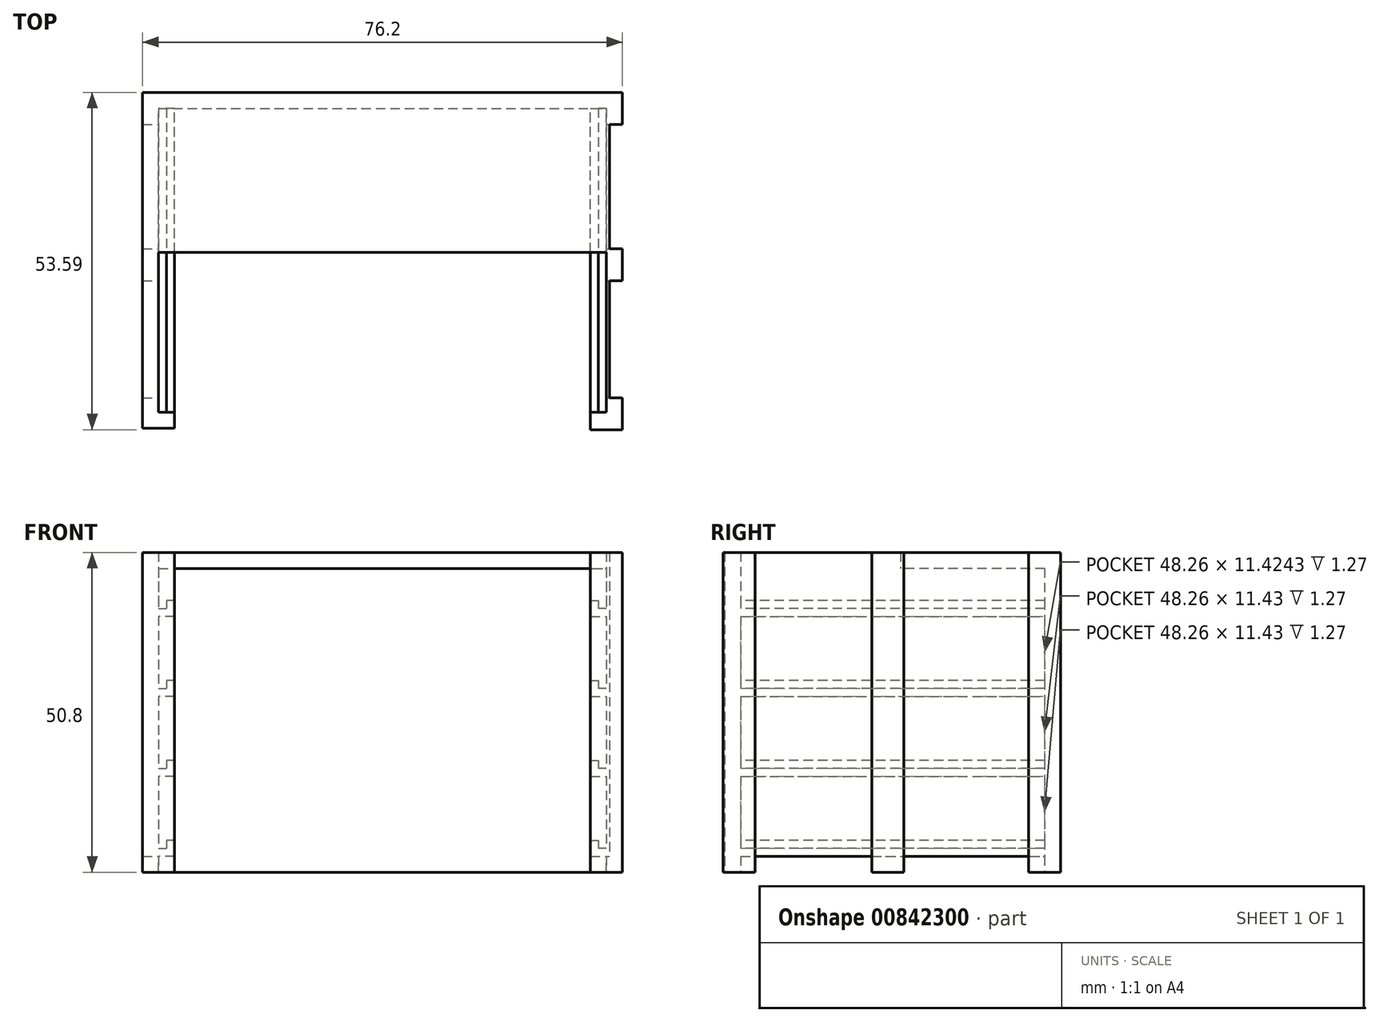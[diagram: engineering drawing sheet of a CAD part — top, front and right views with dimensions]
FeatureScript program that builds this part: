
annotation { "Feature Type Name" : "Feature", "Feature Type Description" : "" }
export const myFeature = defineFeature(function(context is Context, id is Id, definition is map)
    precondition{}
    {
        {
            var Q0;
            Q0=qCreatedBy(makeId("Front.planeOp"),FACE);
            var sketch = newSketch(context, id + "F0", { "sketchPlane" : qUnion([Q0])});
            skLineSegment(sketch, "E0.bottom", {"start": v(-38.1, 29.8) * mm, "end": v(38.1, 29.8) * mm});
            skLineSegment(sketch, "E0.top", {"start": v(-38.1, -21) * mm, "end": v(38.1, -21) * mm});
            skLineSegment(sketch, "E0.left", {"start": v(-38.1, 29.8) * mm, "end": v(-38.1, -21) * mm});
            skLineSegment(sketch, "E0.right", {"start": v(38.1, 29.8) * mm, "end": v(38.1, -21) * mm});
            skSolve(sketch);
        }
        {
            var Q0;
            Q0 = qSketchRegion(id + "F0", true);
            extrude(context, id + "F1", {"entities" : qUnion([Q0]), "depth" : 25.4 * mm, "offsetDistance" : 25.4 * mm, "hasSecondDirection" : true, "secondDirectionOppositeDirection" : true, "secondDirectionDepth" : 25.4 * mm});
        }
        {
            var Q0;
            Q0=makeQuery(id+"F1.opExtrude","CAP_FACE",FACE,{"disambiguationData":[OSD([sQuery(id+"F0.wireOp",EDGE,"E0.bottom"),sQuery(id+"F0.wireOp",EDGE,"E0.top"),sQuery(id+"F0.wireOp",EDGE,"E0.left"),sQuery(id+"F0.wireOp",EDGE,"E0.right")])],"isStart":false});
            var sketch = newSketch(context, id + "F2", { "sketchPlane" : qUnion([Q0])});
            skLineSegment(sketch, "E1.bottom", {"start": v(-35.56, 29.8) * mm, "end": v(35.56, 29.8) * mm});
            skLineSegment(sketch, "E1.top", {"start": v(-35.56, -21) * mm, "end": v(35.56, -21) * mm});
            skLineSegment(sketch, "E1.left", {"start": v(-35.56, 29.8) * mm, "end": v(-35.56, -21) * mm});
            skLineSegment(sketch, "E1.right", {"start": v(35.56, 29.8) * mm, "end": v(35.56, -21) * mm});
            skSolve(sketch);
        }
        {
            var Q0;
            Q0 = qSketchRegion(id + "F2", true);
            extrude(context, id + "F3", {"entities" : qUnion([Q0]), "operationType" : NewBodyOperationType.REMOVE, "oppositeDirection" : true, "depth" : 25.4 * mm, "offsetDistance" : 25.4 * mm});
        }
        {
            var Q0;
            Q0=makeQuery(id+"F3.boolean.opBoolean","COPY",FACE,{"derivedFrom":makeQuery(id+"F3.opExtrude","CAP_FACE",FACE,{"disambiguationData":[OSD([sQuery(id+"F2.wireOp",EDGE,"E1.bottom"),sQuery(id+"F2.wireOp",EDGE,"E1.top"),sQuery(id+"F2.wireOp",EDGE,"E1.left"),sQuery(id+"F2.wireOp",EDGE,"E1.right")])],"isStart":false})});
            var sketch = newSketch(context, id + "F4", { "sketchPlane" : qUnion([Q0])});
            skLineSegment(sketch, "E2.bottom", {"start": v(-35.56, 27.25) * mm, "end": v(35.56, 27.25) * mm});
            skLineSegment(sketch, "E2.top", {"start": v(-35.56, -21) * mm, "end": v(35.56, -21) * mm});
            skLineSegment(sketch, "E2.left", {"start": v(-35.56, 27.25) * mm, "end": v(-35.56, -21) * mm});
            skLineSegment(sketch, "E2.right", {"start": v(35.56, 27.25) * mm, "end": v(35.56, -21) * mm});
            skSolve(sketch);
        }
        {
            var Q0;
            Q0 = qSketchRegion(id + "F4", true);
            extrude(context, id + "F5", {"entities" : qUnion([Q0]), "operationType" : NewBodyOperationType.REMOVE, "oppositeDirection" : true, "depth" : 22.86 * mm, "offsetDistance" : 25.4 * mm});
        }
        {
            var Q0;
            Q0=makeQuery(id+"F5.boolean.opBoolean","MERGE",FACE,{"derivedFrom":[makeQuery(id+"F3.boolean.opBoolean","COPY",FACE,{"derivedFrom":makeQuery(id+"F3.opExtrude","SWEPT_FACE",FACE,{"disambiguationData":[OSD([sQuery(id+"F2.wireOp",EDGE,"E1.left")])]})}),makeQuery(id+"F5.opExtrude","SWEPT_FACE",FACE,{"disambiguationData":[OSD([sQuery(id+"F4.wireOp",EDGE,"E2.left")])]})]});
            var sketch = newSketch(context, id + "F6", { "sketchPlane" : qUnion([Q0])});
            skLineSegment(sketch, "E3.bottom", {"start": v(-25.4, -15.93) * mm, "end": v(22.86, -15.93) * mm});
            skLineSegment(sketch, "E3.top", {"start": v(-25.4, -18.47) * mm, "end": v(22.86, -18.47) * mm});
            skLineSegment(sketch, "E3.left", {"start": v(-25.4, -15.93) * mm, "end": v(-25.4, -18.47) * mm});
            skLineSegment(sketch, "E3.right", {"start": v(22.86, -15.93) * mm, "end": v(22.86, -18.47) * mm});
            skSolve(sketch);
        }
        {
            var Q0;
            Q0 = qSketchRegion(id + "F6", true);
            extrude(context, id + "F7", {"entities" : qUnion([Q0]), "operationType" : NewBodyOperationType.ADD, "depth" : 2.54 * mm, "offsetDistance" : 25.4 * mm});
        }
        {
            var Q0;
            {var subQ0=sQuery(id+"F2.wireOp",EDGE,"E1.left");var subQ1=sQuery(id+"F0.wireOp",EDGE,"E0.bottom");var subQ2=sQuery(id+"F4.wireOp",EDGE,"E2.left");Q0=makeQuery(id+"F7.boolean.opBoolean","SPLIT",FACE,{"disambiguationData":[TD([makeQuery(id+"F1.opExtrude","SWEPT_FACE",FACE,{"disambiguationData":[OSD([subQ1])]})])],"derivedFrom":makeQuery(id+"F5.boolean.opBoolean","MERGE",FACE,{"derivedFrom":[makeQuery(id+"F3.boolean.opBoolean","COPY",FACE,{"derivedFrom":makeQuery(id+"F3.opExtrude","SWEPT_FACE",FACE,{"disambiguationData":[OSD([subQ0])]})}),makeQuery(id+"F5.opExtrude","SWEPT_FACE",FACE,{"disambiguationData":[OSD([subQ2])]})]})});}
            var sketch = newSketch(context, id + "F8", { "sketchPlane" : qUnion([Q0])});
            skLineSegment(sketch, "E4.bottom", {"start": v(-25.4, -3.23) * mm, "end": v(22.86, -3.23) * mm});
            skLineSegment(sketch, "E4.top", {"start": v(-25.4, -5.77) * mm, "end": v(22.86, -5.77) * mm});
            skLineSegment(sketch, "E4.left", {"start": v(-25.4, -3.23) * mm, "end": v(-25.4, -5.77) * mm});
            skLineSegment(sketch, "E4.right", {"start": v(22.86, -3.23) * mm, "end": v(22.86, -5.77) * mm});
            skSolve(sketch);
        }
        {
            var Q0;
            Q0 = qSketchRegion(id + "F8", true);
            extrude(context, id + "F9", {"entities" : qUnion([Q0]), "operationType" : NewBodyOperationType.ADD, "depth" : 2.54 * mm, "offsetDistance" : 25.4 * mm});
        }
        {
            var Q0;
            {var subQ0=sQuery(id+"F2.wireOp",EDGE,"E1.left");var subQ2=sQuery(id+"F0.wireOp",EDGE,"E0.bottom");var subQ4=sQuery(id+"F4.wireOp",EDGE,"E2.left");var subQ8=makeQuery(id+"F1.opExtrude","SWEPT_FACE",FACE,{"disambiguationData":[OSD([subQ2])]});Q0=makeQuery(id+"F9.boolean.opBoolean","SPLIT",FACE,{"disambiguationData":[TD([subQ8])],"derivedFrom":makeQuery(id+"F7.boolean.opBoolean","SPLIT",FACE,{"disambiguationData":[TD([subQ8])],"derivedFrom":makeQuery(id+"F5.boolean.opBoolean","MERGE",FACE,{"derivedFrom":[makeQuery(id+"F3.boolean.opBoolean","COPY",FACE,{"derivedFrom":makeQuery(id+"F3.opExtrude","SWEPT_FACE",FACE,{"disambiguationData":[OSD([subQ0])]})}),makeQuery(id+"F5.opExtrude","SWEPT_FACE",FACE,{"disambiguationData":[OSD([subQ4])]})]})})});}
            var sketch = newSketch(context, id + "F10", { "sketchPlane" : qUnion([Q0])});
            skLineSegment(sketch, "E5.bottom", {"start": v(-25.4, 9.47) * mm, "end": v(22.86, 9.47) * mm});
            skLineSegment(sketch, "E5.top", {"start": v(-25.4, 6.93) * mm, "end": v(22.86, 6.93) * mm});
            skLineSegment(sketch, "E5.left", {"start": v(-25.4, 9.47) * mm, "end": v(-25.4, 6.93) * mm});
            skLineSegment(sketch, "E5.right", {"start": v(22.86, 9.47) * mm, "end": v(22.86, 6.93) * mm});
            skSolve(sketch);
        }
        {
            var Q0;
            Q0 = qSketchRegion(id + "F10", true);
            extrude(context, id + "F11", {"entities" : qUnion([Q0]), "operationType" : NewBodyOperationType.ADD, "depth" : 2.54 * mm, "offsetDistance" : 25.4 * mm});
        }
        {
            var Q0;
            {var subQ0=sQuery(id+"F2.wireOp",EDGE,"E1.left");var subQ2=sQuery(id+"F0.wireOp",EDGE,"E0.bottom");var subQ4=sQuery(id+"F4.wireOp",EDGE,"E2.left");var subQ8=makeQuery(id+"F1.opExtrude","SWEPT_FACE",FACE,{"disambiguationData":[OSD([subQ2])]});Q0=makeQuery(id+"F11.boolean.opBoolean","SPLIT",FACE,{"disambiguationData":[TD([subQ8])],"derivedFrom":makeQuery(id+"F9.boolean.opBoolean","SPLIT",FACE,{"disambiguationData":[TD([subQ8])],"derivedFrom":makeQuery(id+"F7.boolean.opBoolean","SPLIT",FACE,{"disambiguationData":[TD([subQ8])],"derivedFrom":makeQuery(id+"F5.boolean.opBoolean","MERGE",FACE,{"derivedFrom":[makeQuery(id+"F3.boolean.opBoolean","COPY",FACE,{"derivedFrom":makeQuery(id+"F3.opExtrude","SWEPT_FACE",FACE,{"disambiguationData":[OSD([subQ0])]})}),makeQuery(id+"F5.opExtrude","SWEPT_FACE",FACE,{"disambiguationData":[OSD([subQ4])]})]})})})});}
            var sketch = newSketch(context, id + "F12", { "sketchPlane" : qUnion([Q0])});
            skLineSegment(sketch, "E6.bottom", {"start": v(-25.4, 22.17) * mm, "end": v(22.86, 22.17) * mm});
            skLineSegment(sketch, "E6.top", {"start": v(-25.4, 19.63) * mm, "end": v(22.86, 19.63) * mm});
            skLineSegment(sketch, "E6.left", {"start": v(-25.4, 22.17) * mm, "end": v(-25.4, 19.63) * mm});
            skLineSegment(sketch, "E6.right", {"start": v(22.86, 22.17) * mm, "end": v(22.86, 19.63) * mm});
            skSolve(sketch);
        }
        {
            var Q0;
            Q0 = qSketchRegion(id + "F12", true);
            extrude(context, id + "F13", {"entities" : qUnion([Q0]), "operationType" : NewBodyOperationType.ADD, "depth" : 2.54 * mm, "offsetDistance" : 25.4 * mm});
        }
        {
            var Q0;
            Q0=makeQuery(id+"F1.opExtrude","SWEPT_BODY",BODY,{"disambiguationData":[OSD([sQuery(id+"F0.wireOp",EDGE,"E0.bottom"),sQuery(id+"F0.wireOp",EDGE,"E0.top"),sQuery(id+"F0.wireOp",EDGE,"E0.left"),sQuery(id+"F0.wireOp",EDGE,"E0.right")])]});
            var Q1;
            Q1=qCreatedBy(makeId("Right.planeOp"),FACE);
            mirror(context, id + "F14", {"operationType" : NewBodyOperationType.ADD, "entities" : qUnion([Q0]), "mirrorPlane" : qUnion([Q1])});
        }
        {
            var Q0;
            {var subQ0=sQuery(id+"F0.wireOp",EDGE,"E0.bottom");var subQ1=sQuery(id+"F0.wireOp",EDGE,"E0.top");var subQ2=sQuery(id+"F0.wireOp",EDGE,"E0.left");Q0=makeQuery(id+"F13.boolean.opBoolean","MERGE",FACE,{"derivedFrom":[makeQuery(id+"F11.boolean.opBoolean","MERGE",FACE,{"derivedFrom":[makeQuery(id+"F9.boolean.opBoolean","MERGE",FACE,{"derivedFrom":[makeQuery(id+"F7.boolean.opBoolean","MERGE",FACE,{"derivedFrom":[makeQuery(id+"F3.boolean.opBoolean","SPLIT",FACE,{"disambiguationData":[TD([makeQuery(id+"F1.opExtrude","SWEPT_FACE",FACE,{"disambiguationData":[OSD([subQ2])]})])],"derivedFrom":makeQuery(id+"F1.opExtrude","CAP_FACE",FACE,{"disambiguationData":[OSD([subQ0,subQ1,subQ2,sQuery(id+"F0.wireOp",EDGE,"E0.right")])],"isStart":false})}),makeQuery(id+"F7.opExtrude","SWEPT_FACE",FACE,{"disambiguationData":[OSD([sQuery(id+"F6.wireOp",EDGE,"E3.left")])]})]}),makeQuery(id+"F9.opExtrude","SWEPT_FACE",FACE,{"disambiguationData":[OSD([sQuery(id+"F8.wireOp",EDGE,"E4.left")])]})]}),makeQuery(id+"F11.opExtrude","SWEPT_FACE",FACE,{"disambiguationData":[OSD([sQuery(id+"F10.wireOp",EDGE,"E5.left")])]})]}),makeQuery(id+"F13.opExtrude","SWEPT_FACE",FACE,{"disambiguationData":[OSD([sQuery(id+"F12.wireOp",EDGE,"E6.left")])]})]});}
            var sketch = newSketch(context, id + "F15", { "sketchPlane" : qUnion([Q0])});
            skLineSegment(sketch, "E7.bottom", {"start": v(-35.56, -15.93) * mm, "end": v(-34.3, -15.93) * mm});
            skLineSegment(sketch, "E7.top", {"start": v(-35.56, -17.2) * mm, "end": v(-34.3, -17.2) * mm});
            skLineSegment(sketch, "E7.left", {"start": v(-35.56, -15.93) * mm, "end": v(-35.56, -17.2) * mm});
            skLineSegment(sketch, "E7.right", {"start": v(-34.3, -15.93) * mm, "end": v(-34.3, -17.2) * mm});
            skSolve(sketch);
        }
        {
            var Q0;
            Q0 = qSketchRegion(id + "F15", true);
            extrude(context, id + "F16", {"entities" : qUnion([Q0]), "operationType" : NewBodyOperationType.REMOVE, "oppositeDirection" : true, "depth" : 48.26 * mm, "offsetDistance" : 25.4 * mm});
        }
        {
            var Q0;
            {var subQ0=sQuery(id+"F0.wireOp",EDGE,"E0.bottom");var subQ1=sQuery(id+"F0.wireOp",EDGE,"E0.top");var subQ2=sQuery(id+"F0.wireOp",EDGE,"E0.left");Q0=makeQuery(id+"F13.boolean.opBoolean","MERGE",FACE,{"derivedFrom":[makeQuery(id+"F11.boolean.opBoolean","MERGE",FACE,{"derivedFrom":[makeQuery(id+"F9.boolean.opBoolean","MERGE",FACE,{"derivedFrom":[makeQuery(id+"F7.boolean.opBoolean","MERGE",FACE,{"derivedFrom":[makeQuery(id+"F3.boolean.opBoolean","SPLIT",FACE,{"disambiguationData":[TD([makeQuery(id+"F1.opExtrude","SWEPT_FACE",FACE,{"disambiguationData":[OSD([subQ2])]})])],"derivedFrom":makeQuery(id+"F1.opExtrude","CAP_FACE",FACE,{"disambiguationData":[OSD([subQ0,subQ1,subQ2,sQuery(id+"F0.wireOp",EDGE,"E0.right")])],"isStart":false})}),makeQuery(id+"F7.opExtrude","SWEPT_FACE",FACE,{"disambiguationData":[OSD([sQuery(id+"F6.wireOp",EDGE,"E3.left")])]})]}),makeQuery(id+"F9.opExtrude","SWEPT_FACE",FACE,{"disambiguationData":[OSD([sQuery(id+"F8.wireOp",EDGE,"E4.left")])]})]}),makeQuery(id+"F11.opExtrude","SWEPT_FACE",FACE,{"disambiguationData":[OSD([sQuery(id+"F10.wireOp",EDGE,"E5.left")])]})]}),makeQuery(id+"F13.opExtrude","SWEPT_FACE",FACE,{"disambiguationData":[OSD([sQuery(id+"F12.wireOp",EDGE,"E6.left")])]})]});}
            var sketch = newSketch(context, id + "F17", { "sketchPlane" : qUnion([Q0])});
            skLineSegment(sketch, "E8.bottom", {"start": v(-35.56, -3.23) * mm, "end": v(-34.3, -3.23) * mm});
            skLineSegment(sketch, "E8.top", {"start": v(-35.56, -4.5) * mm, "end": v(-34.3, -4.5) * mm});
            skLineSegment(sketch, "E8.left", {"start": v(-35.56, -3.23) * mm, "end": v(-35.56, -4.5) * mm});
            skLineSegment(sketch, "E8.right", {"start": v(-34.3, -3.23) * mm, "end": v(-34.3, -4.5) * mm});
            skSolve(sketch);
        }
        {
            var Q0;
            Q0 = qSketchRegion(id + "F17", true);
            extrude(context, id + "F18", {"entities" : qUnion([Q0]), "operationType" : NewBodyOperationType.REMOVE, "oppositeDirection" : true, "depth" : 48.26 * mm, "offsetDistance" : 25.4 * mm});
        }
        {
            var Q0;
            {var subQ0=sQuery(id+"F0.wireOp",EDGE,"E0.bottom");var subQ1=sQuery(id+"F0.wireOp",EDGE,"E0.top");var subQ2=sQuery(id+"F0.wireOp",EDGE,"E0.left");Q0=makeQuery(id+"F13.boolean.opBoolean","MERGE",FACE,{"derivedFrom":[makeQuery(id+"F11.boolean.opBoolean","MERGE",FACE,{"derivedFrom":[makeQuery(id+"F9.boolean.opBoolean","MERGE",FACE,{"derivedFrom":[makeQuery(id+"F7.boolean.opBoolean","MERGE",FACE,{"derivedFrom":[makeQuery(id+"F3.boolean.opBoolean","SPLIT",FACE,{"disambiguationData":[TD([makeQuery(id+"F1.opExtrude","SWEPT_FACE",FACE,{"disambiguationData":[OSD([subQ2])]})])],"derivedFrom":makeQuery(id+"F1.opExtrude","CAP_FACE",FACE,{"disambiguationData":[OSD([subQ0,subQ1,subQ2,sQuery(id+"F0.wireOp",EDGE,"E0.right")])],"isStart":false})}),makeQuery(id+"F7.opExtrude","SWEPT_FACE",FACE,{"disambiguationData":[OSD([sQuery(id+"F6.wireOp",EDGE,"E3.left")])]})]}),makeQuery(id+"F9.opExtrude","SWEPT_FACE",FACE,{"disambiguationData":[OSD([sQuery(id+"F8.wireOp",EDGE,"E4.left")])]})]}),makeQuery(id+"F11.opExtrude","SWEPT_FACE",FACE,{"disambiguationData":[OSD([sQuery(id+"F10.wireOp",EDGE,"E5.left")])]})]}),makeQuery(id+"F13.opExtrude","SWEPT_FACE",FACE,{"disambiguationData":[OSD([sQuery(id+"F12.wireOp",EDGE,"E6.left")])]})]});}
            var sketch = newSketch(context, id + "F19", { "sketchPlane" : qUnion([Q0])});
            skPoint(sketch, "E9.oppositeSnap0", {"position": v(-34.3, 9.47) * mm});
            skLineSegment(sketch, "E9.bottom", {"start": v(-35.56, 9.47) * mm, "end": v(-34.3, 9.47) * mm});
            skLineSegment(sketch, "E9.top", {"start": v(-35.56, 8.2) * mm, "end": v(-34.3, 8.2) * mm});
            skLineSegment(sketch, "E9.left", {"start": v(-35.56, 9.47) * mm, "end": v(-35.56, 8.2) * mm});
            skLineSegment(sketch, "E9.right", {"start": v(-34.3, 9.47) * mm, "end": v(-34.3, 8.2) * mm});
            skSolve(sketch);
        }
        {
            var Q0;
            Q0 = qSketchRegion(id + "F19", true);
            extrude(context, id + "F20", {"entities" : qUnion([Q0]), "operationType" : NewBodyOperationType.REMOVE, "oppositeDirection" : true, "depth" : 48.26 * mm, "offsetDistance" : 25.4 * mm});
        }
        {
            var Q0;
            {var subQ0=sQuery(id+"F0.wireOp",EDGE,"E0.bottom");var subQ1=sQuery(id+"F0.wireOp",EDGE,"E0.top");var subQ2=sQuery(id+"F0.wireOp",EDGE,"E0.left");Q0=makeQuery(id+"F13.boolean.opBoolean","MERGE",FACE,{"derivedFrom":[makeQuery(id+"F11.boolean.opBoolean","MERGE",FACE,{"derivedFrom":[makeQuery(id+"F9.boolean.opBoolean","MERGE",FACE,{"derivedFrom":[makeQuery(id+"F7.boolean.opBoolean","MERGE",FACE,{"derivedFrom":[makeQuery(id+"F3.boolean.opBoolean","SPLIT",FACE,{"disambiguationData":[TD([makeQuery(id+"F1.opExtrude","SWEPT_FACE",FACE,{"disambiguationData":[OSD([subQ2])]})])],"derivedFrom":makeQuery(id+"F1.opExtrude","CAP_FACE",FACE,{"disambiguationData":[OSD([subQ0,subQ1,subQ2,sQuery(id+"F0.wireOp",EDGE,"E0.right")])],"isStart":false})}),makeQuery(id+"F7.opExtrude","SWEPT_FACE",FACE,{"disambiguationData":[OSD([sQuery(id+"F6.wireOp",EDGE,"E3.left")])]})]}),makeQuery(id+"F9.opExtrude","SWEPT_FACE",FACE,{"disambiguationData":[OSD([sQuery(id+"F8.wireOp",EDGE,"E4.left")])]})]}),makeQuery(id+"F11.opExtrude","SWEPT_FACE",FACE,{"disambiguationData":[OSD([sQuery(id+"F10.wireOp",EDGE,"E5.left")])]})]}),makeQuery(id+"F13.opExtrude","SWEPT_FACE",FACE,{"disambiguationData":[OSD([sQuery(id+"F12.wireOp",EDGE,"E6.left")])]})]});}
            var sketch = newSketch(context, id + "F21", { "sketchPlane" : qUnion([Q0])});
            skPoint(sketch, "E10.oppositeSnap0", {"position": v(-34.3, 22.17) * mm});
            skLineSegment(sketch, "E10.bottom", {"start": v(-35.56, 22.17) * mm, "end": v(-34.3, 22.17) * mm});
            skLineSegment(sketch, "E10.top", {"start": v(-35.56, 20.9) * mm, "end": v(-34.3, 20.9) * mm});
            skLineSegment(sketch, "E10.left", {"start": v(-35.56, 22.17) * mm, "end": v(-35.56, 20.9) * mm});
            skLineSegment(sketch, "E10.right", {"start": v(-34.3, 22.17) * mm, "end": v(-34.3, 20.9) * mm});
            skSolve(sketch);
        }
        {
            var Q0;
            Q0 = qSketchRegion(id + "F21", true);
            extrude(context, id + "F22", {"entities" : qUnion([Q0]), "operationType" : NewBodyOperationType.REMOVE, "oppositeDirection" : true, "depth" : 48.26 * mm, "offsetDistance" : 25.4 * mm});
        }
        {
            var Q0;
            {var subQ0=sQuery(id+"F0.wireOp",EDGE,"E0.bottom");var subQ2=sQuery(id+"F0.wireOp",EDGE,"E0.top");var subQ4=sQuery(id+"F0.wireOp",EDGE,"E0.left");var subQ5=sQuery(id+"F0.wireOp",EDGE,"E0.right");var subQ6=makeQuery(id+"F1.opExtrude","CAP_FACE",FACE,{"disambiguationData":[OSD([subQ0,subQ2,subQ4,subQ5])],"isStart":false});Q0=makeQuery(id+"F14.boolean.opBoolean","MERGE",FACE,{"derivedFrom":[makeQuery(id+"F3.boolean.opBoolean","SPLIT",FACE,{"disambiguationData":[TD([makeQuery(id+"F1.opExtrude","SWEPT_FACE",FACE,{"disambiguationData":[OSD([subQ5])]})])],"derivedFrom":subQ6}),makeQuery(id+"F14.opPattern","COPY",FACE,{"derivedFrom":makeQuery(id+"F13.boolean.opBoolean","MERGE",FACE,{"derivedFrom":[makeQuery(id+"F11.boolean.opBoolean","MERGE",FACE,{"derivedFrom":[makeQuery(id+"F9.boolean.opBoolean","MERGE",FACE,{"derivedFrom":[makeQuery(id+"F7.boolean.opBoolean","MERGE",FACE,{"derivedFrom":[makeQuery(id+"F3.boolean.opBoolean","SPLIT",FACE,{"disambiguationData":[TD([makeQuery(id+"F1.opExtrude","SWEPT_FACE",FACE,{"disambiguationData":[OSD([subQ4])]})])],"derivedFrom":subQ6}),makeQuery(id+"F7.opExtrude","SWEPT_FACE",FACE,{"disambiguationData":[OSD([sQuery(id+"F6.wireOp",EDGE,"E3.left")])]})]}),makeQuery(id+"F9.opExtrude","SWEPT_FACE",FACE,{"disambiguationData":[OSD([sQuery(id+"F8.wireOp",EDGE,"E4.left")])]})]}),makeQuery(id+"F11.opExtrude","SWEPT_FACE",FACE,{"disambiguationData":[OSD([sQuery(id+"F10.wireOp",EDGE,"E5.left")])]})]}),makeQuery(id+"F13.opExtrude","SWEPT_FACE",FACE,{"disambiguationData":[OSD([sQuery(id+"F12.wireOp",EDGE,"E6.left")])]})]}),"instanceName":"1"})]});}
            var sketch = newSketch(context, id + "F23", { "sketchPlane" : qUnion([Q0])});
            skLineSegment(sketch, "E11.bottom", {"start": v(35.56, 22.17) * mm, "end": v(34.3, 22.17) * mm});
            skLineSegment(sketch, "E11.top", {"start": v(35.56, 20.9) * mm, "end": v(34.3, 20.9) * mm});
            skLineSegment(sketch, "E11.left", {"start": v(35.56, 22.17) * mm, "end": v(35.56, 20.9) * mm});
            skLineSegment(sketch, "E11.right", {"start": v(34.3, 22.17) * mm, "end": v(34.3, 20.9) * mm});
            skSolve(sketch);
        }
        {
            var Q0;
            Q0 = qSketchRegion(id + "F23", true);
            extrude(context, id + "F24", {"entities" : qUnion([Q0]), "operationType" : NewBodyOperationType.REMOVE, "oppositeDirection" : true, "depth" : 48.26 * mm, "offsetDistance" : 25.4 * mm});
        }
        {
            var Q0;
            {var subQ0=sQuery(id+"F0.wireOp",EDGE,"E0.bottom");var subQ2=sQuery(id+"F0.wireOp",EDGE,"E0.top");var subQ4=sQuery(id+"F0.wireOp",EDGE,"E0.left");var subQ5=sQuery(id+"F0.wireOp",EDGE,"E0.right");var subQ6=makeQuery(id+"F1.opExtrude","CAP_FACE",FACE,{"disambiguationData":[OSD([subQ0,subQ2,subQ4,subQ5])],"isStart":false});Q0=makeQuery(id+"F14.boolean.opBoolean","MERGE",FACE,{"derivedFrom":[makeQuery(id+"F3.boolean.opBoolean","SPLIT",FACE,{"disambiguationData":[TD([makeQuery(id+"F1.opExtrude","SWEPT_FACE",FACE,{"disambiguationData":[OSD([subQ5])]})])],"derivedFrom":subQ6}),makeQuery(id+"F14.opPattern","COPY",FACE,{"derivedFrom":makeQuery(id+"F13.boolean.opBoolean","MERGE",FACE,{"derivedFrom":[makeQuery(id+"F11.boolean.opBoolean","MERGE",FACE,{"derivedFrom":[makeQuery(id+"F9.boolean.opBoolean","MERGE",FACE,{"derivedFrom":[makeQuery(id+"F7.boolean.opBoolean","MERGE",FACE,{"derivedFrom":[makeQuery(id+"F3.boolean.opBoolean","SPLIT",FACE,{"disambiguationData":[TD([makeQuery(id+"F1.opExtrude","SWEPT_FACE",FACE,{"disambiguationData":[OSD([subQ4])]})])],"derivedFrom":subQ6}),makeQuery(id+"F7.opExtrude","SWEPT_FACE",FACE,{"disambiguationData":[OSD([sQuery(id+"F6.wireOp",EDGE,"E3.left")])]})]}),makeQuery(id+"F9.opExtrude","SWEPT_FACE",FACE,{"disambiguationData":[OSD([sQuery(id+"F8.wireOp",EDGE,"E4.left")])]})]}),makeQuery(id+"F11.opExtrude","SWEPT_FACE",FACE,{"disambiguationData":[OSD([sQuery(id+"F10.wireOp",EDGE,"E5.left")])]})]}),makeQuery(id+"F13.opExtrude","SWEPT_FACE",FACE,{"disambiguationData":[OSD([sQuery(id+"F12.wireOp",EDGE,"E6.left")])]})]}),"instanceName":"1"})]});}
            var sketch = newSketch(context, id + "F25", { "sketchPlane" : qUnion([Q0])});
            skLineSegment(sketch, "E12.bottom", {"start": v(35.56, 9.47) * mm, "end": v(34.3, 9.47) * mm});
            skLineSegment(sketch, "E12.top", {"start": v(35.56, 8.2) * mm, "end": v(34.3, 8.2) * mm});
            skLineSegment(sketch, "E12.left", {"start": v(35.56, 9.47) * mm, "end": v(35.56, 8.2) * mm});
            skLineSegment(sketch, "E12.right", {"start": v(34.3, 9.47) * mm, "end": v(34.3, 8.2) * mm});
            skSolve(sketch);
        }
        {
            var Q0;
            Q0 = qSketchRegion(id + "F25", true);
            extrude(context, id + "F26", {"entities" : qUnion([Q0]), "operationType" : NewBodyOperationType.REMOVE, "oppositeDirection" : true, "depth" : 48.26 * mm, "offsetDistance" : 25.4 * mm});
        }
        {
            var Q0;
            {var subQ0=sQuery(id+"F0.wireOp",EDGE,"E0.bottom");var subQ2=sQuery(id+"F0.wireOp",EDGE,"E0.top");var subQ4=sQuery(id+"F0.wireOp",EDGE,"E0.left");var subQ5=sQuery(id+"F0.wireOp",EDGE,"E0.right");var subQ6=makeQuery(id+"F1.opExtrude","CAP_FACE",FACE,{"disambiguationData":[OSD([subQ0,subQ2,subQ4,subQ5])],"isStart":false});Q0=makeQuery(id+"F14.boolean.opBoolean","MERGE",FACE,{"derivedFrom":[makeQuery(id+"F3.boolean.opBoolean","SPLIT",FACE,{"disambiguationData":[TD([makeQuery(id+"F1.opExtrude","SWEPT_FACE",FACE,{"disambiguationData":[OSD([subQ5])]})])],"derivedFrom":subQ6}),makeQuery(id+"F14.opPattern","COPY",FACE,{"derivedFrom":makeQuery(id+"F13.boolean.opBoolean","MERGE",FACE,{"derivedFrom":[makeQuery(id+"F11.boolean.opBoolean","MERGE",FACE,{"derivedFrom":[makeQuery(id+"F9.boolean.opBoolean","MERGE",FACE,{"derivedFrom":[makeQuery(id+"F7.boolean.opBoolean","MERGE",FACE,{"derivedFrom":[makeQuery(id+"F3.boolean.opBoolean","SPLIT",FACE,{"disambiguationData":[TD([makeQuery(id+"F1.opExtrude","SWEPT_FACE",FACE,{"disambiguationData":[OSD([subQ4])]})])],"derivedFrom":subQ6}),makeQuery(id+"F7.opExtrude","SWEPT_FACE",FACE,{"disambiguationData":[OSD([sQuery(id+"F6.wireOp",EDGE,"E3.left")])]})]}),makeQuery(id+"F9.opExtrude","SWEPT_FACE",FACE,{"disambiguationData":[OSD([sQuery(id+"F8.wireOp",EDGE,"E4.left")])]})]}),makeQuery(id+"F11.opExtrude","SWEPT_FACE",FACE,{"disambiguationData":[OSD([sQuery(id+"F10.wireOp",EDGE,"E5.left")])]})]}),makeQuery(id+"F13.opExtrude","SWEPT_FACE",FACE,{"disambiguationData":[OSD([sQuery(id+"F12.wireOp",EDGE,"E6.left")])]})]}),"instanceName":"1"})]});}
            var sketch = newSketch(context, id + "F27", { "sketchPlane" : qUnion([Q0])});
            skLineSegment(sketch, "E13.bottom", {"start": v(35.56, -3.23) * mm, "end": v(34.3, -3.23) * mm});
            skLineSegment(sketch, "E13.top", {"start": v(35.56, -4.5) * mm, "end": v(34.3, -4.5) * mm});
            skLineSegment(sketch, "E13.left", {"start": v(35.56, -3.23) * mm, "end": v(35.56, -4.5) * mm});
            skLineSegment(sketch, "E13.right", {"start": v(34.3, -3.23) * mm, "end": v(34.3, -4.5) * mm});
            skSolve(sketch);
        }
        {
            var Q0;
            Q0 = qSketchRegion(id + "F27", true);
            extrude(context, id + "F28", {"entities" : qUnion([Q0]), "operationType" : NewBodyOperationType.REMOVE, "oppositeDirection" : true, "depth" : 48.26 * mm, "offsetDistance" : 25.4 * mm});
        }
        {
            var Q0;
            {var subQ0=sQuery(id+"F0.wireOp",EDGE,"E0.bottom");var subQ2=sQuery(id+"F0.wireOp",EDGE,"E0.top");var subQ4=sQuery(id+"F0.wireOp",EDGE,"E0.left");var subQ5=sQuery(id+"F0.wireOp",EDGE,"E0.right");var subQ6=makeQuery(id+"F1.opExtrude","CAP_FACE",FACE,{"disambiguationData":[OSD([subQ0,subQ2,subQ4,subQ5])],"isStart":false});Q0=makeQuery(id+"F14.boolean.opBoolean","MERGE",FACE,{"derivedFrom":[makeQuery(id+"F3.boolean.opBoolean","SPLIT",FACE,{"disambiguationData":[TD([makeQuery(id+"F1.opExtrude","SWEPT_FACE",FACE,{"disambiguationData":[OSD([subQ5])]})])],"derivedFrom":subQ6}),makeQuery(id+"F14.opPattern","COPY",FACE,{"derivedFrom":makeQuery(id+"F13.boolean.opBoolean","MERGE",FACE,{"derivedFrom":[makeQuery(id+"F11.boolean.opBoolean","MERGE",FACE,{"derivedFrom":[makeQuery(id+"F9.boolean.opBoolean","MERGE",FACE,{"derivedFrom":[makeQuery(id+"F7.boolean.opBoolean","MERGE",FACE,{"derivedFrom":[makeQuery(id+"F3.boolean.opBoolean","SPLIT",FACE,{"disambiguationData":[TD([makeQuery(id+"F1.opExtrude","SWEPT_FACE",FACE,{"disambiguationData":[OSD([subQ4])]})])],"derivedFrom":subQ6}),makeQuery(id+"F7.opExtrude","SWEPT_FACE",FACE,{"disambiguationData":[OSD([sQuery(id+"F6.wireOp",EDGE,"E3.left")])]})]}),makeQuery(id+"F9.opExtrude","SWEPT_FACE",FACE,{"disambiguationData":[OSD([sQuery(id+"F8.wireOp",EDGE,"E4.left")])]})]}),makeQuery(id+"F11.opExtrude","SWEPT_FACE",FACE,{"disambiguationData":[OSD([sQuery(id+"F10.wireOp",EDGE,"E5.left")])]})]}),makeQuery(id+"F13.opExtrude","SWEPT_FACE",FACE,{"disambiguationData":[OSD([sQuery(id+"F12.wireOp",EDGE,"E6.left")])]})]}),"instanceName":"1"})]});}
            var sketch = newSketch(context, id + "F29", { "sketchPlane" : qUnion([Q0])});
            skPoint(sketch, "E14.oppositeSnap0", {"position": v(34.3, -18.47) * mm});
            skLineSegment(sketch, "E14.bottom", {"start": v(35.56, -15.93) * mm, "end": v(34.3, -15.93) * mm});
            skLineSegment(sketch, "E14.top", {"start": v(35.56, -17.2) * mm, "end": v(34.3, -17.2) * mm});
            skLineSegment(sketch, "E14.left", {"start": v(35.56, -15.93) * mm, "end": v(35.56, -17.2) * mm});
            skLineSegment(sketch, "E14.right", {"start": v(34.3, -15.93) * mm, "end": v(34.3, -17.2) * mm});
            skSolve(sketch);
        }
        {
            var Q0;
            Q0 = qSketchRegion(id + "F29", true);
            extrude(context, id + "F30", {"entities" : qUnion([Q0]), "operationType" : NewBodyOperationType.REMOVE, "oppositeDirection" : true, "depth" : 48.26 * mm, "offsetDistance" : 25.4 * mm});
        }
        {
            var Q0;
            {var subQ0=sQuery(id+"F0.wireOp",EDGE,"E0.bottom");var subQ2=sQuery(id+"F0.wireOp",EDGE,"E0.top");var subQ4=sQuery(id+"F0.wireOp",EDGE,"E0.left");var subQ5=sQuery(id+"F0.wireOp",EDGE,"E0.right");var subQ6=makeQuery(id+"F1.opExtrude","CAP_FACE",FACE,{"disambiguationData":[OSD([subQ0,subQ2,subQ4,subQ5])],"isStart":false});Q0=makeQuery(id+"F14.boolean.opBoolean","MERGE",FACE,{"derivedFrom":[makeQuery(id+"F3.boolean.opBoolean","SPLIT",FACE,{"disambiguationData":[TD([makeQuery(id+"F1.opExtrude","SWEPT_FACE",FACE,{"disambiguationData":[OSD([subQ5])]})])],"derivedFrom":subQ6}),makeQuery(id+"F14.opPattern","COPY",FACE,{"derivedFrom":makeQuery(id+"F13.boolean.opBoolean","MERGE",FACE,{"derivedFrom":[makeQuery(id+"F11.boolean.opBoolean","MERGE",FACE,{"derivedFrom":[makeQuery(id+"F9.boolean.opBoolean","MERGE",FACE,{"derivedFrom":[makeQuery(id+"F7.boolean.opBoolean","MERGE",FACE,{"derivedFrom":[makeQuery(id+"F3.boolean.opBoolean","SPLIT",FACE,{"disambiguationData":[TD([makeQuery(id+"F1.opExtrude","SWEPT_FACE",FACE,{"disambiguationData":[OSD([subQ4])]})])],"derivedFrom":subQ6}),makeQuery(id+"F7.opExtrude","SWEPT_FACE",FACE,{"disambiguationData":[OSD([sQuery(id+"F6.wireOp",EDGE,"E3.left")])]})]}),makeQuery(id+"F9.opExtrude","SWEPT_FACE",FACE,{"disambiguationData":[OSD([sQuery(id+"F8.wireOp",EDGE,"E4.left")])]})]}),makeQuery(id+"F11.opExtrude","SWEPT_FACE",FACE,{"disambiguationData":[OSD([sQuery(id+"F10.wireOp",EDGE,"E5.left")])]})]}),makeQuery(id+"F13.opExtrude","SWEPT_FACE",FACE,{"disambiguationData":[OSD([sQuery(id+"F12.wireOp",EDGE,"E6.left")])]})]}),"instanceName":"1"})]});}
            var sketch = newSketch(context, id + "F31", { "sketchPlane" : qUnion([Q0])});
            skLineSegment(sketch, "E15.bottom", {"start": v(38.1, 29.8) * mm, "end": v(33.02, 29.8) * mm});
            skLineSegment(sketch, "E15.top", {"start": v(38.1, -21) * mm, "end": v(33.02, -21) * mm});
            skLineSegment(sketch, "E15.left", {"start": v(38.1, 29.8) * mm, "end": v(38.1, -21) * mm});
            skLineSegment(sketch, "E15.right", {"start": v(33.02, 29.8) * mm, "end": v(33.02, -21) * mm});
            skSolve(sketch);
        }
        {
            var Q0;
            Q0 = qSketchRegion(id + "F31", true);
            extrude(context, id + "F32", {"entities" : qUnion([Q0]), "operationType" : NewBodyOperationType.ADD, "depth" : 2.8 * mm, "offsetDistance" : 25.4 * mm});
        }
        {
            var Q0;
            {var subQ0=sQuery(id+"F0.wireOp",EDGE,"E0.bottom");var subQ1=sQuery(id+"F0.wireOp",EDGE,"E0.top");var subQ2=sQuery(id+"F0.wireOp",EDGE,"E0.left");Q0=makeQuery(id+"F13.boolean.opBoolean","MERGE",FACE,{"derivedFrom":[makeQuery(id+"F11.boolean.opBoolean","MERGE",FACE,{"derivedFrom":[makeQuery(id+"F9.boolean.opBoolean","MERGE",FACE,{"derivedFrom":[makeQuery(id+"F7.boolean.opBoolean","MERGE",FACE,{"derivedFrom":[makeQuery(id+"F3.boolean.opBoolean","SPLIT",FACE,{"disambiguationData":[TD([makeQuery(id+"F1.opExtrude","SWEPT_FACE",FACE,{"disambiguationData":[OSD([subQ2])]})])],"derivedFrom":makeQuery(id+"F1.opExtrude","CAP_FACE",FACE,{"disambiguationData":[OSD([subQ0,subQ1,subQ2,sQuery(id+"F0.wireOp",EDGE,"E0.right")])],"isStart":false})}),makeQuery(id+"F7.opExtrude","SWEPT_FACE",FACE,{"disambiguationData":[OSD([sQuery(id+"F6.wireOp",EDGE,"E3.left")])]})]}),makeQuery(id+"F9.opExtrude","SWEPT_FACE",FACE,{"disambiguationData":[OSD([sQuery(id+"F8.wireOp",EDGE,"E4.left")])]})]}),makeQuery(id+"F11.opExtrude","SWEPT_FACE",FACE,{"disambiguationData":[OSD([sQuery(id+"F10.wireOp",EDGE,"E5.left")])]})]}),makeQuery(id+"F13.opExtrude","SWEPT_FACE",FACE,{"disambiguationData":[OSD([sQuery(id+"F12.wireOp",EDGE,"E6.left")])]})]});}
            var sketch = newSketch(context, id + "F33", { "sketchPlane" : qUnion([Q0])});
            skLineSegment(sketch, "E16.bottom", {"start": v(-38.1, 29.8) * mm, "end": v(-33.02, 29.8) * mm});
            skLineSegment(sketch, "E16.top", {"start": v(-38.1, -21) * mm, "end": v(-33.02, -21) * mm});
            skLineSegment(sketch, "E16.left", {"start": v(-38.1, 29.8) * mm, "end": v(-38.1, -21) * mm});
            skLineSegment(sketch, "E16.right", {"start": v(-33.02, 29.8) * mm, "end": v(-33.02, -21) * mm});
            skSolve(sketch);
        }
        {
            var Q0;
            Q0 = qSketchRegion(id + "F33", true);
            extrude(context, id + "F34", {"entities" : qUnion([Q0]), "operationType" : NewBodyOperationType.ADD, "depth" : 2.54 * mm, "offsetDistance" : 25.4 * mm});
        }
        {
            var Q0;
            Q0=makeQuery(id+"F32.boolean.opBoolean","MERGE",FACE,{"derivedFrom":[makeQuery(id+"F1.opExtrude","SWEPT_FACE",FACE,{"disambiguationData":[OSD([sQuery(id+"F0.wireOp",EDGE,"E0.right")])]}),makeQuery(id+"F32.opExtrude","SWEPT_FACE",FACE,{"disambiguationData":[OSD([sQuery(id+"F31.wireOp",EDGE,"E15.left")])]})]});
            var sketch = newSketch(context, id + "F35", { "sketchPlane" : qUnion([Q0])});
            skLineSegment(sketch, "E17.bottom", {"start": v(-23.11, 29.8) * mm, "end": v(-4.56, 29.8) * mm});
            skLineSegment(sketch, "E17.top", {"start": v(-23.11, -21) * mm, "end": v(-4.56, -21) * mm});
            skLineSegment(sketch, "E17.left", {"start": v(-23.11, 29.8) * mm, "end": v(-23.11, -21) * mm});
            skLineSegment(sketch, "E17.right", {"start": v(-4.56, 29.8) * mm, "end": v(-4.56, -21) * mm});
            skLineSegment(sketch, "E18.bottom", {"start": v(0.52, 29.8) * mm, "end": v(20.32, 29.8) * mm});
            skLineSegment(sketch, "E18.top", {"start": v(0.52, -21) * mm, "end": v(20.32, -21) * mm});
            skLineSegment(sketch, "E18.left", {"start": v(0.52, 29.8) * mm, "end": v(0.52, -21) * mm});
            skLineSegment(sketch, "E18.right", {"start": v(20.32, 29.8) * mm, "end": v(20.32, -21) * mm});
            skSolve(sketch);
        }
        {
            var Q0;
            Q0 = qSketchRegion(id + "F35", true);
            extrude(context, id + "F36", {"entities" : qUnion([Q0]), "operationType" : NewBodyOperationType.REMOVE, "oppositeDirection" : true, "depth" : 2.03 * mm, "offsetDistance" : 25.4 * mm});
        }
        {
            var Q0;
            Q0=makeQuery(id+"F36.boolean.opBoolean","COPY",FACE,{"derivedFrom":makeQuery(id+"F36.opExtrude","CAP_FACE",FACE,{"disambiguationData":[OSD([sQuery(id+"F35.wireOp",EDGE,"E17.bottom"),sQuery(id+"F35.wireOp",EDGE,"E17.top"),sQuery(id+"F35.wireOp",EDGE,"E17.left"),sQuery(id+"F35.wireOp",EDGE,"E17.right")])],"isStart":false})});
            var sketch = newSketch(context, id + "F37", { "sketchPlane" : qUnion([Q0])});
            skLineSegment(sketch, "E19.bottom", {"start": v(-23.11, -21) * mm, "end": v(-4.56, -21) * mm});
            skLineSegment(sketch, "E19.top", {"start": v(-23.11, -18.47) * mm, "end": v(-4.56, -18.47) * mm});
            skLineSegment(sketch, "E19.left", {"start": v(-23.11, -21) * mm, "end": v(-23.11, -18.47) * mm});
            skLineSegment(sketch, "E19.right", {"start": v(-4.56, -21) * mm, "end": v(-4.56, -18.47) * mm});
            skSolve(sketch);
        }
        {
            var Q0;
            Q0 = qSketchRegion(id + "F37", true);
            extrude(context, id + "F38", {"entities" : qUnion([Q0]), "operationType" : NewBodyOperationType.REMOVE, "endBound" : BoundingType.THROUGH_ALL, "oppositeDirection" : true, "depth" : 25.4 * mm, "offsetDistance" : 25.4 * mm});
        }
        {
            var Q0;
            Q0=makeQuery(id+"F36.boolean.opBoolean","COPY",FACE,{"derivedFrom":makeQuery(id+"F36.opExtrude","CAP_FACE",FACE,{"disambiguationData":[OSD([sQuery(id+"F35.wireOp",EDGE,"E18.bottom"),sQuery(id+"F35.wireOp",EDGE,"E18.top"),sQuery(id+"F35.wireOp",EDGE,"E18.left"),sQuery(id+"F35.wireOp",EDGE,"E18.right")])],"isStart":false})});
            var sketch = newSketch(context, id + "F39", { "sketchPlane" : qUnion([Q0])});
            skLineSegment(sketch, "E20.bottom", {"start": v(0.52, -21) * mm, "end": v(20.32, -21) * mm});
            skLineSegment(sketch, "E20.top", {"start": v(0.52, -18.47) * mm, "end": v(20.32, -18.47) * mm});
            skLineSegment(sketch, "E20.left", {"start": v(0.52, -21) * mm, "end": v(0.52, -18.47) * mm});
            skLineSegment(sketch, "E20.right", {"start": v(20.32, -21) * mm, "end": v(20.32, -18.47) * mm});
            skSolve(sketch);
        }
        {
            var Q0;
            Q0 = qSketchRegion(id + "F39", true);
            extrude(context, id + "F40", {"entities" : qUnion([Q0]), "operationType" : NewBodyOperationType.REMOVE, "endBound" : BoundingType.THROUGH_ALL, "oppositeDirection" : true, "depth" : 25.4 * mm, "offsetDistance" : 25.4 * mm});
        }
    });
